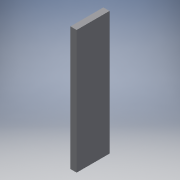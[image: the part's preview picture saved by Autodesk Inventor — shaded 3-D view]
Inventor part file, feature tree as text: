
AUTODESK INVENTOR PART (.ipt)
format: ipt  version: 2016 (Build 200138000, 138)  size: 88,576 bytes
history: native  units: in
note: dims shown in document units (in); Inventor stores cm internally (conversion verified against a paired STEP export)
features: sketch x2, extrude x1
ambient origin geometry x8: Origin, YZ Plane, XZ Plane, XY Plane, X Axis, Y Axis, Z Axis, Center Point
bodies: Solid1 (feature_tree)
feature tree (3):
  extrude  "Extrusion1"  Depth=3.0in
  sketch  "Sketch2"  dims[d2=0.8in d3=0.0in]
  sketch  "Sketch1"  dims[d0=0.15in d1=3.0in]
